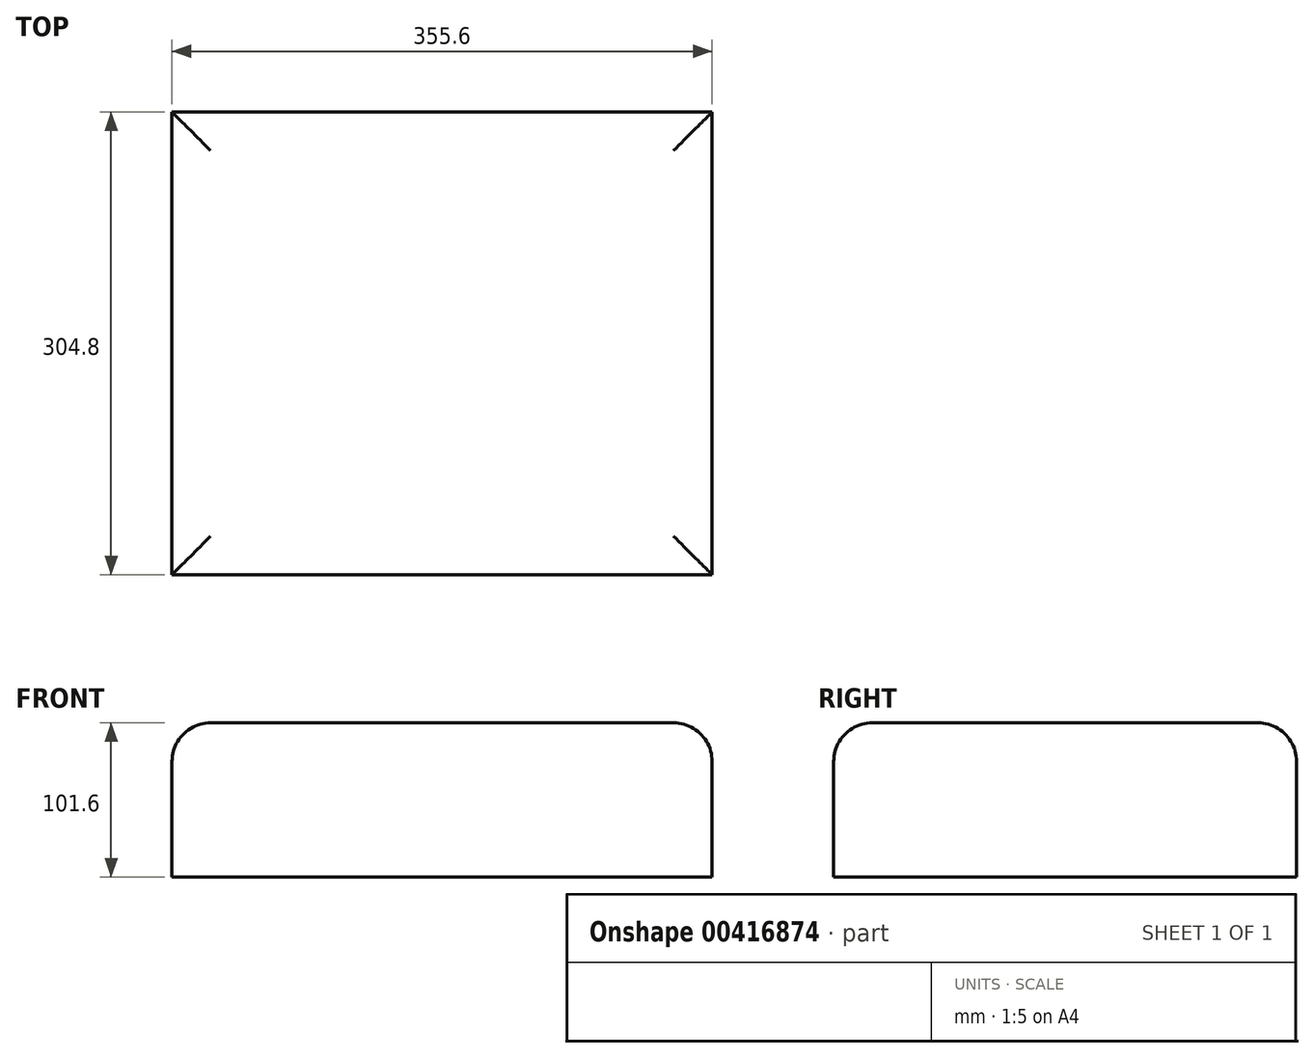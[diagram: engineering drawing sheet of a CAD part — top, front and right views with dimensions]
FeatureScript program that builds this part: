
annotation { "Feature Type Name" : "Feature", "Feature Type Description" : "" }
export const myFeature = defineFeature(function(context is Context, id is Id, definition is map)
    precondition{}
    {
        {
            var Q0;
            Q0=qCreatedBy(makeId("Top.planeOp"),FACE);
            var sketch = newSketch(context, id + "F0", { "sketchPlane" : qUnion([Q0])});
            skLineSegment(sketch, "E0.bottom", {"start": v(-177.8, 152.4) * mm, "end": v(177.8, 152.4) * mm});
            skLineSegment(sketch, "E0.top", {"start": v(-177.8, -152.4) * mm, "end": v(177.8, -152.4) * mm});
            skLineSegment(sketch, "E0.left", {"start": v(-177.8, 152.4) * mm, "end": v(-177.8, -152.4) * mm});
            skLineSegment(sketch, "E0.right", {"start": v(177.8, 152.4) * mm, "end": v(177.8, -152.4) * mm});
            skPoint(sketch, "E0.middle", {"position": v(0, 0) * mm});
            skSolve(sketch);
        }
        {
            var Q0;
            Q0 = qSketchRegion(id + "F0", true);
            extrude(context, id + "F1", {"entities" : qUnion([Q0]), "depth" : 25.4 * mm});
        }
        {
            var Q0;
            Q0=makeQuery(id+"F1.opExtrude","CAP_FACE",FACE,{"disambiguationData":[OSD([sQuery(id+"F0.wireOp",EDGE,"E0.bottom"),sQuery(id+"F0.wireOp",EDGE,"E0.top"),sQuery(id+"F0.wireOp",EDGE,"E0.left"),sQuery(id+"F0.wireOp",EDGE,"E0.right")])],"isStart":false});
            var sketch = newSketch(context, id + "F2", { "sketchPlane" : qUnion([Q0])});
            skLineSegment(sketch, "E1.bottom", {"start": v(-177.8, 152.4) * mm, "end": v(177.8, 152.4) * mm});
            skLineSegment(sketch, "E1.top", {"start": v(-177.8, -152.4) * mm, "end": v(177.8, -152.4) * mm});
            skLineSegment(sketch, "E1.left", {"start": v(-177.8, 152.4) * mm, "end": v(-177.8, -152.4) * mm});
            skLineSegment(sketch, "E1.right", {"start": v(177.8, 152.4) * mm, "end": v(177.8, -152.4) * mm});
            skPoint(sketch, "E1.middle", {"position": v(0, 0) * mm});
            skSolve(sketch);
        }
        {
            var Q0;
            Q0 = qSketchRegion(id + "F2", true);
            extrude(context, id + "F3", {"entities" : qUnion([Q0]), "operationType" : NewBodyOperationType.ADD, "depth" : 76.2 * mm});
        }
        {
            var Q0;
            Q0=makeQuery(id+"F3.opExtrude","CAP_EDGE",EDGE,{"disambiguationData":[OSD([sQuery(id+"F2.wireOp",EDGE,"E1.left")])],"isStart":false});
            var Q1;
            Q1=makeQuery(id+"F3.opExtrude","CAP_EDGE",EDGE,{"disambiguationData":[OSD([sQuery(id+"F2.wireOp",EDGE,"E1.top")])],"isStart":false});
            var Q2;
            Q2=makeQuery(id+"F3.opExtrude","CAP_EDGE",EDGE,{"disambiguationData":[OSD([sQuery(id+"F2.wireOp",EDGE,"E1.right")])],"isStart":false});
            var Q3;
            Q3=makeQuery(id+"F3.opExtrude","CAP_EDGE",EDGE,{"disambiguationData":[OSD([sQuery(id+"F2.wireOp",EDGE,"E1.bottom")])],"isStart":false});
            fillet(context, id + "F4", {"entities" : qUnion([Q0, Q1, Q2, Q3]), "radius" : 25.4 * mm, "tangentPropagation" : true, "allowEdgeOverflow" : false});
        }
    });
